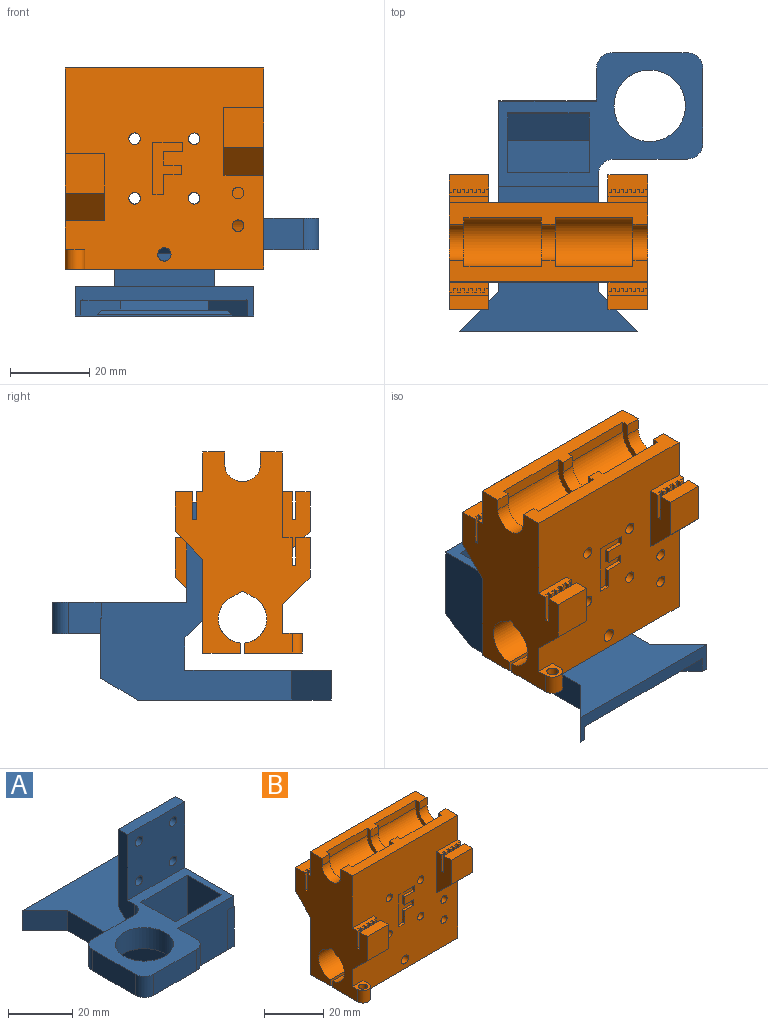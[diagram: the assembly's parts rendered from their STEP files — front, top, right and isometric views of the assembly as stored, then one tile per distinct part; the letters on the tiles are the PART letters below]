
ASSEMBLY  parts=2 mates=1
PART A: 52 faces, bbox 61.4x70.2x49.6 mm
  f0: plane 15.13x2.75mm, normal (0,-1,0), area 40mm2, adj f1,f4,f16,f31,f42,f43
  f1: plane 2.35x0.1mm, normal (0,0,1), area 0.2mm2, adj f0,f4,f12,f43
  f2: plane 49.63x48.05mm, normal (1,0,0), area 828.1mm2, adj f3,f11,f12,f14,f15,f21,f25,f26
  f3: plane 51.4x33.8mm, normal (0,0,1), area 683.6mm2, adj f2,f12,f13,f14,f16,f22,f23,f24
  f4: plane 15.13x0.1mm, normal (1,0,0), area 1.5mm2, adj f0,f1,f12,f30
  f5: plane 15.13x0.1mm, normal (-1,0,0), area 1.5mm2, adj f12,f25,f30,f41
  f6: plane 10x10mm, normal (-0.71,0.71,0), area 61.9mm2, adj f7,f8,f28,f29,f34,f38,f39,f40
  f7: plane 51.13x34mm, normal (0,0,-1), area 853.3mm2, adj f6,f9,f13,f22,f23,f24,f27,f28
  f8: plane 31.51x30.04mm, normal (0,0,1), area 683.5mm2, adj f6,f27,f28,f32,f36,f39
  f9: plane 22x7.11mm, normal (0,0.51,0.86), area 182.2mm2, adj f7,f10,f27,f28
  f10: plane 22x11.17mm, normal (0,0,1), area 245.7mm2, adj f9,f27,f28,f32
  f11: plane 25x8.13mm, normal (0,1,0), area 203.1mm2, adj f2,f16,f26,f37
  f12: plane 24.6x19.13mm, normal (0,-1,0), area 393.3mm2, adj f1,f2,f3,f4,f5,f30,f41,f43
  f13: plane 20.5x19.13mm, normal (0,-1,0), area 392.1mm2, adj f3,f7,f22,f23
  f14: plane 25x25mm, normal (0,-1,0), area 589.7mm2, adj f2,f3,f15,f16,f17,f18,f19,f20
  f15: plane 25x4mm, normal (0,0,1), area 100mm2, adj f2,f14,f16,f21
  f16: plane 49.63x48.05mm, normal (-1,0,0), area 678.9mm2, adj f0,f3,f11,f14,f15,f21,f26,f29
  f17: cylinder r=1.68mm len=4mm, axis (0,1,0), area 42.1mm2, adj f14,f21
  f18: cylinder r=1.68mm len=4mm, axis (0,1,0), area 42.1mm2, adj f14,f21
  f19: cylinder r=1.68mm len=4mm, axis (0,1,0), area 42.1mm2, adj f14,f21
  f20: cylinder r=1.68mm len=4mm, axis (0,1,0), area 42.1mm2, adj f14,f21
  f21: plane 29.5x25mm, normal (0,1,0), area 702.2mm2, adj f2,f15,f16,f17,f18,f19,f20,f37
  f22: plane 19.13x15mm, normal (1,0,0), area 286.9mm2, adj f3,f7,f13,f24
  f23: plane 19.13x15mm, normal (-1,0,0), area 286.9mm2, adj f3,f7,f13,f24
  f24: plane 20.5x19.13mm, normal (0,1,0), area 392.1mm2, adj f3,f7,f22,f23
  f25: plane 15.13x2.75mm, normal (0,-1,0), area 41.6mm2, adj f2,f5,f31,f41
  f26: plane 45x36.85mm, normal (0,0,1), area 1021.3mm2, adj f2,f11,f16,f33,f34,f35
  f27: plane 45.13x4.25mm, normal (1,0,0), area 170.1mm2, adj f7,f8,f9,f10,f32,f36
  f28: plane 45.13x4.25mm, normal (-1,0,0), area 170.1mm2, adj f6,f7,f8,f9,f10,f32
  f29: plane 48.85x45mm, normal (0,0,-1), area 1167.7mm2, adj f2,f6,f16,f31,f33,f34,f35,f36
  f30: plane 19.5x0.1mm, normal (0,0,1), area 1.9mm2, adj f4,f5,f12,f31
  f31: plane 25x9.2mm, normal (0,-0.51,-0.86), area 268mm2, adj f0,f2,f16,f25,f29,f30
  f32: cylinder r=5mm len=22mm, axis (-1,0,0), area 34.9mm2, adj f8,f10,f27,f28
  f33: plane 10x10mm, normal (0.71,-0.71,0), area 106.1mm2, adj f2,f26,f29,f34
  f34: plane 45x7.5mm, normal (0,1,0), area 169.5mm2, adj f6,f26,f29,f33,f35,f36,f40
  f35: plane 10x10mm, normal (-0.71,-0.71,0), area 106.1mm2, adj f16,f26,f29,f34
  f36: plane 10x10mm, normal (0.71,0.71,0), area 61.9mm2, adj f7,f8,f27,f29,f34,f38,f39,f40
  f37: plane 25x4.5mm, normal (0,0.71,-0.71), area 159.1mm2, adj f2,f11,f16,f21
  f38: plane 33.91x0.3mm, normal (0,1,0), area 10.2mm2, adj f6,f29,f36,f39
  f39: plane 33.91x1.2mm, normal (0,0.71,0.71), area 55.5mm2, adj f6,f8,f36,f38
  f40: plane 42x4mm, normal (0,-0.35,-0.94), area 162.3mm2, adj f6,f7,f34,f36
  f41: plane 2.75x0.1mm, normal (0,0,1), area 0.3mm2, adj f2,f5,f12,f25
  f42: plane 30.8x26.8mm, normal (0,0,-1), area 451mm2, adj f0,f16,f43,f44,f45,f46,f47,f48
  f43: plane 8.2x8mm, normal (1,0,0), area 65.2mm2, adj f0,f1,f3,f12,f42,f51
  f44: plane 18.4x8mm, normal (0,1,0), area 147.2mm2, adj f3,f42,f48,f49
  f45: plane 18.8x8mm, normal (-1,0,0), area 150.4mm2, adj f3,f42,f49,f50
  f46: cylinder r=9mm len=18mm, axis (0,0,1), area 452.4mm2, adj f3,f42
  f47: plane 18.8x8mm, normal (0,-1,0), area 150.4mm2, adj f3,f42,f50,f51
  f48: cylinder r=4mm len=8mm, axis (0,0,-1), area 50.3mm2, adj f3,f16,f42,f44
  f49: cylinder r=4mm len=8mm, axis (0,0,-1), area 50.3mm2, adj f3,f42,f44,f45
  f50: cylinder r=4mm len=8mm, axis (0,0,1), area 50.3mm2, adj f3,f42,f45,f47
  f51: cylinder r=4mm len=8mm, axis (0,0,-1), area 50.3mm2, adj f3,f42,f43,f47
PART B: 162 faces, bbox 50x34x50.6 mm
  f0: plane 50.6x50mm, normal (0,-1,0), area 2059.2mm2, adj f1,f6,f7,f8,f22,f24,f25,f40
  f1: plane 50.6x34mm, normal (-1,0,0), area 1020.9mm2, adj f0,f2,f5,f8,f12,f23,f24,f25
  f2: plane 10x4.5mm, normal (0,0,1), area 40.5mm2, adj f1,f91,f92,f114,f115,f116,f117,f118
  f3: plane 17x7mm, normal (-1,0,0), area 88.2mm2, adj f4,f5,f88,f89,f105,f106,f113,f135
  f4: plane 10x4.5mm, normal (0,0,1), area 40.5mm2, adj f3,f22,f89,f93,f94,f95,f96,f97
  f5: plane 50.6x50mm, normal (0,1,0), area 2154.8mm2, adj f1,f3,f12,f22,f23,f88,f90,f91
  f6: plane 10x2.5mm, normal (0,0,1), area 20.5mm2, adj f0,f7,f22,f67,f68,f69,f70,f71
  f7: plane 17x7mm, normal (-1,0,0), area 88.2mm2, adj f0,f6,f42,f43,f44,f79,f80,f87
  f8: plane 10x2.5mm, normal (0,0,1), area 20.5mm2, adj f0,f1,f40,f46,f47,f48,f49,f50
  f9: plane 19.5x3mm, normal (0,-1,0), area 58.5mm2, adj f10,f12,f34,f38
  f10: cylinder r=6.2mm len=19.5mm, axis (-1,0,0), area 379.8mm2, adj f9,f11,f34,f38
  f11: plane 19.5x3mm, normal (0,1,0), area 58.5mm2, adj f10,f25,f34,f38
  f12: plane 50x5.5mm, normal (0,0,1), area 208.7mm2, adj f1,f5,f9,f13,f16,f21,f22,f32
  f13: plane 3.5x3mm, normal (0,-1,0), area 10.5mm2, adj f12,f15,f33,f34
  f14: plane 3.5x3mm, normal (0,1,0), area 10.5mm2, adj f15,f25,f33,f34
  f15: cylinder r=4.5mm len=9mm, axis (-1,0,0), area 49.5mm2, adj f13,f14,f33,f34
  f16: plane 19.5x3mm, normal (0,-1,0), area 58.5mm2, adj f12,f17,f32,f33
  f17: cylinder r=6.2mm len=19.5mm, axis (-1,0,0), area 379.8mm2, adj f16,f18,f32,f33
  f18: plane 19.5x3mm, normal (0,1,0), area 58.5mm2, adj f17,f25,f32,f33
  f19: cylinder r=4.5mm len=9mm, axis (-1,0,0), area 53mm2, adj f20,f21,f22,f32
  f20: plane 3.75x3mm, normal (0,1,0), area 11.2mm2, adj f19,f22,f25,f32
  f21: plane 3.75x3mm, normal (0,-1,0), area 11.2mm2, adj f12,f19,f22,f32
  f22: plane 50.6x34mm, normal (1,0,0), area 995.8mm2, adj f0,f4,f5,f6,f12,f19,f20,f21
  f23: plane 50x9.5mm, normal (0,0,-1), area 475mm2, adj f1,f5,f22,f30
  f24: plane 50x14.5mm, normal (0,0,-1), area 490.7mm2, adj f0,f1,f22,f31,f159,f160,f161
  f25: plane 50x5.5mm, normal (0,0,1), area 208.7mm2, adj f0,f1,f11,f14,f18,f20,f22,f32
  f26: plane 50x2.45mm, normal (0,-0.5,-0.87), area 141.3mm2, adj f1,f22,f27,f29
  f27: cylinder r=6.1mm len=50mm, axis (-1,0,0), area 791.2mm2, adj f1,f22,f26,f30,f139
  f28: cylinder r=6.1mm len=50mm, axis (-1,0,0), area 784.5mm2, adj f1,f22,f29,f31,f138,f143,f144
  f29: plane 50x2.45mm, normal (0,0.5,-0.87), area 141.3mm2, adj f1,f22,f26,f28
  f30: plane 50x2.52mm, normal (0,-1,0), area 125.2mm2, adj f1,f22,f23,f27,f139
  f31: plane 50x2.52mm, normal (0,1,0), area 125.2mm2, adj f1,f22,f24,f28,f138
  f32: plane 12.4x9.2mm, normal (-1,0,0), area 38.8mm2, adj f12,f16,f17,f18,f19,f20,f21,f25
  f33: plane 12.4x9.2mm, normal (1,0,0), area 38.8mm2, adj f12,f13,f14,f15,f16,f17,f18,f25
  f34: plane 12.4x9.2mm, normal (-1,0,0), area 38.8mm2, adj f9,f10,f11,f12,f13,f14,f15,f25
  f35: plane 3.75x3mm, normal (0,-1,0), area 11.2mm2, adj f1,f12,f37,f38
  f36: plane 3.75x3mm, normal (0,1,0), area 11.2mm2, adj f1,f25,f37,f38
  f37: cylinder r=4.5mm len=9mm, axis (-1,0,0), area 53mm2, adj f1,f35,f36,f38
  f38: plane 12.4x9.2mm, normal (1,0,0), area 38.8mm2, adj f9,f10,f11,f12,f25,f35,f36,f37
  f39: plane 10x3.6mm, normal (0,0,1), area 36mm2, adj f1,f40,f41,f59
  f40: plane 17x7mm, normal (1,0,0), area 81.9mm2, adj f0,f8,f39,f41,f45,f59,f60,f66
  f41: plane 10x10mm, normal (0,-1,0), area 100mm2, adj f1,f39,f40,f45
  f42: plane 10x3.6mm, normal (0,0,1), area 36mm2, adj f7,f22,f43,f80
  f43: plane 10x10mm, normal (0,-1,0), area 100mm2, adj f7,f22,f42,f44
  f44: plane 10x7mm, normal (0,-0.71,-0.71), area 99mm2, adj f0,f7,f22,f43
  f45: plane 10x7mm, normal (0,-0.71,-0.71), area 99mm2, adj f0,f1,f40,f41
  f46: plane 7x1mm, normal (0,-1,0), area 7mm2, adj f8,f47,f65,f66
  f47: plane 7x0.9mm, normal (-1,0,0), area 6.3mm2, adj f8,f46,f48,f66
  f48: plane 7x1mm, normal (0,-1,0), area 7mm2, adj f8,f47,f49,f66
  f49: plane 7x0.9mm, normal (1,0,0), area 6.3mm2, adj f8,f48,f50,f66
  f50: plane 7x1mm, normal (0,-1,0), area 7mm2, adj f8,f49,f51,f66
  f51: plane 7x0.9mm, normal (-1,0,0), area 6.3mm2, adj f8,f50,f52,f66
  f52: plane 7x1mm, normal (0,-1,0), area 7mm2, adj f8,f51,f53,f66
  f53: plane 7x0.9mm, normal (1,0,0), area 6.3mm2, adj f8,f52,f54,f66
  f54: plane 7x1mm, normal (0,-1,0), area 7mm2, adj f8,f53,f55,f66
  f55: plane 7x0.9mm, normal (-1,0,0), area 6.3mm2, adj f8,f54,f56,f66
  f56: plane 7x1mm, normal (0,-1,0), area 7mm2, adj f8,f55,f57,f66
  f57: plane 7x0.9mm, normal (1,0,0), area 6.3mm2, adj f8,f56,f58,f66
  f58: plane 7x1mm, normal (0,-1,0), area 7mm2, adj f1,f8,f57,f66
  f59: plane 10x7mm, normal (0,1,0), area 70mm2, adj f1,f39,f40,f66
  f60: plane 7x1mm, normal (0,-1,0), area 7mm2, adj f8,f40,f61,f66
  f61: plane 7x0.9mm, normal (1,0,0), area 6.3mm2, adj f8,f60,f62,f66
  f62: plane 7x1mm, normal (0,-1,0), area 7mm2, adj f8,f61,f63,f66
  f63: plane 7x0.9mm, normal (-1,0,0), area 6.3mm2, adj f8,f62,f64,f66
  f64: plane 7x1mm, normal (0,-1,0), area 7mm2, adj f8,f63,f65,f66
  f65: plane 7x0.9mm, normal (1,0,0), area 6.3mm2, adj f8,f46,f64,f66
  f66: plane 10x1.8mm, normal (0,0,1), area 13.5mm2, adj f1,f40,f46,f47,f48,f49,f50,f51
  f67: plane 7x1mm, normal (0,-1,0), area 7mm2, adj f6,f68,f86,f87
  f68: plane 7x0.9mm, normal (-1,0,0), area 6.3mm2, adj f6,f67,f69,f87
  f69: plane 7x1mm, normal (0,-1,0), area 7mm2, adj f6,f68,f70,f87
  f70: plane 7x0.9mm, normal (1,0,0), area 6.3mm2, adj f6,f69,f71,f87
  f71: plane 7x1mm, normal (0,-1,0), area 7mm2, adj f6,f70,f72,f87
  f72: plane 7x0.9mm, normal (-1,0,0), area 6.3mm2, adj f6,f71,f73,f87
  f73: plane 7x1mm, normal (0,-1,0), area 7mm2, adj f6,f72,f74,f87
  f74: plane 7x0.9mm, normal (1,0,0), area 6.3mm2, adj f6,f73,f75,f87
  f75: plane 7x1mm, normal (0,-1,0), area 7mm2, adj f6,f74,f76,f87
  f76: plane 7x0.9mm, normal (-1,0,0), area 6.3mm2, adj f6,f75,f77,f87
  f77: plane 7x1mm, normal (0,-1,0), area 7mm2, adj f6,f76,f78,f87
  f78: plane 7x0.9mm, normal (1,0,0), area 6.3mm2, adj f6,f77,f79,f87
  f79: plane 7x1mm, normal (0,-1,0), area 7mm2, adj f6,f7,f78,f87
  f80: plane 10x7mm, normal (0,1,0), area 70mm2, adj f7,f22,f42,f87
  f81: plane 7x1mm, normal (0,-1,0), area 7mm2, adj f6,f22,f82,f87
  f82: plane 7x0.9mm, normal (1,0,0), area 6.3mm2, adj f6,f81,f83,f87
  f83: plane 7x1mm, normal (0,-1,0), area 7mm2, adj f6,f82,f84,f87
  f84: plane 7x0.9mm, normal (-1,0,0), area 6.3mm2, adj f6,f83,f85,f87
  f85: plane 7x1mm, normal (0,-1,0), area 7mm2, adj f6,f84,f86,f87
  f86: plane 7x0.9mm, normal (1,0,0), area 6.3mm2, adj f6,f67,f85,f87
  f87: plane 10x1.8mm, normal (0,0,1), area 13.5mm2, adj f7,f22,f67,f68,f69,f70,f71,f72
  f88: plane 10x1.6mm, normal (0,0,1), area 16mm2, adj f3,f5,f22,f106
  f89: plane 10x10mm, normal (0,1,0), area 100mm2, adj f3,f4,f22,f135
  f90: plane 10x1.6mm, normal (0,0,1), area 16mm2, adj f1,f5,f91,f127
  f91: plane 17x7mm, normal (1,0,0), area 81.9mm2, adj f2,f5,f90,f92,f127,f128,f134,f136
  f92: plane 10x10mm, normal (0,1,0), area 100mm2, adj f1,f2,f91,f136
  f93: plane 7x1mm, normal (0,-1,0), area 7mm2, adj f4,f94,f112,f113
  f94: plane 7x0.9mm, normal (-1,0,0), area 6.3mm2, adj f4,f93,f95,f113
  f95: plane 7x1mm, normal (0,-1,0), area 7mm2, adj f4,f94,f96,f113
  f96: plane 7x0.9mm, normal (1,0,0), area 6.3mm2, adj f4,f95,f97,f113
  f97: plane 7x1mm, normal (0,-1,0), area 7mm2, adj f4,f96,f98,f113
  f98: plane 7x0.9mm, normal (-1,0,0), area 6.3mm2, adj f4,f97,f99,f113
  f99: plane 7x1mm, normal (0,-1,0), area 7mm2, adj f4,f98,f100,f113
  f100: plane 7x0.9mm, normal (1,0,0), area 6.3mm2, adj f4,f99,f101,f113
  f101: plane 7x1mm, normal (0,-1,0), area 7mm2, adj f4,f100,f102,f113
  f102: plane 7x0.9mm, normal (-1,0,0), area 6.3mm2, adj f4,f101,f103,f113
  f103: plane 7x1mm, normal (0,-1,0), area 7mm2, adj f4,f102,f104,f113
  f104: plane 7x0.9mm, normal (1,0,0), area 6.3mm2, adj f4,f103,f105,f113
  f105: plane 7x1mm, normal (0,-1,0), area 7mm2, adj f3,f4,f104,f113
  f106: plane 10x7mm, normal (0,1,0), area 70mm2, adj f3,f22,f88,f113
  f107: plane 7x1mm, normal (0,-1,0), area 7mm2, adj f4,f22,f108,f113
  f108: plane 7x0.9mm, normal (1,0,0), area 6.3mm2, adj f4,f107,f109,f113
  f109: plane 7x1mm, normal (0,-1,0), area 7mm2, adj f4,f108,f110,f113
  f110: plane 7x0.9mm, normal (-1,0,0), area 6.3mm2, adj f4,f109,f111,f113
  f111: plane 7x1mm, normal (0,-1,0), area 7mm2, adj f4,f110,f112,f113
  f112: plane 7x0.9mm, normal (1,0,0), area 6.3mm2, adj f4,f93,f111,f113
  f113: plane 10x1.8mm, normal (0,0,1), area 13.5mm2, adj f3,f22,f93,f94,f95,f96,f97,f98
  f114: plane 7x1mm, normal (0,-1,0), area 7mm2, adj f2,f115,f133,f134
  f115: plane 7x0.9mm, normal (-1,0,0), area 6.3mm2, adj f2,f114,f116,f134
  f116: plane 7x1mm, normal (0,-1,0), area 7mm2, adj f2,f115,f117,f134
  f117: plane 7x0.9mm, normal (1,0,0), area 6.3mm2, adj f2,f116,f118,f134
  f118: plane 7x1mm, normal (0,-1,0), area 7mm2, adj f2,f117,f119,f134
  f119: plane 7x0.9mm, normal (-1,0,0), area 6.3mm2, adj f2,f118,f120,f134
  f120: plane 7x1mm, normal (0,-1,0), area 7mm2, adj f2,f119,f121,f134
  f121: plane 7x0.9mm, normal (1,0,0), area 6.3mm2, adj f2,f120,f122,f134
  f122: plane 7x1mm, normal (0,-1,0), area 7mm2, adj f2,f121,f123,f134
  f123: plane 7x0.9mm, normal (-1,0,0), area 6.3mm2, adj f2,f122,f124,f134
  f124: plane 7x1mm, normal (0,-1,0), area 7mm2, adj f2,f123,f125,f134
  f125: plane 7x0.9mm, normal (1,0,0), area 6.3mm2, adj f2,f124,f126,f134
  f126: plane 7x1mm, normal (0,-1,0), area 7mm2, adj f1,f2,f125,f134
  f127: plane 10x7mm, normal (0,1,0), area 70mm2, adj f1,f90,f91,f134
  f128: plane 7x1mm, normal (0,-1,0), area 7mm2, adj f2,f91,f129,f134
  f129: plane 7x0.9mm, normal (1,0,0), area 6.3mm2, adj f2,f128,f130,f134
  f130: plane 7x1mm, normal (0,-1,0), area 7mm2, adj f2,f129,f131,f134
  f131: plane 7x0.9mm, normal (-1,0,0), area 6.3mm2, adj f2,f130,f132,f134
  f132: plane 7x1mm, normal (0,-1,0), area 7mm2, adj f2,f131,f133,f134
  f133: plane 7x0.9mm, normal (1,0,0), area 6.3mm2, adj f2,f114,f132,f134
  f134: plane 10x1.8mm, normal (0,0,1), area 13.5mm2, adj f1,f91,f114,f115,f116,f117,f118,f119
  f135: plane 10x7mm, normal (0,0.71,-0.71), area 99mm2, adj f3,f5,f22,f89
  f136: plane 10x7mm, normal (0,0.71,-0.71), area 99mm2, adj f1,f5,f91,f92
  f137: cylinder r=1.45mm len=20mm, axis (0,-1,0), area 182.2mm2, adj f0,f5
  f138: cylinder r=1.68mm len=9.5mm, axis (0,-1,0), area 73.2mm2, adj f0,f28,f31
  f139: cylinder r=1.68mm len=9.5mm, axis (0,-1,0), area 73.1mm2, adj f5,f27,f30
  f140: cylinder r=1.45mm len=20mm, axis (0,-1,0), area 182.2mm2, adj f0,f5
  f141: cylinder r=1.45mm len=20mm, axis (0,-1,0), area 182.2mm2, adj f0,f5
  f142: cylinder r=1.45mm len=20mm, axis (0,-1,0), area 182.2mm2, adj f0,f5
  f143: cylinder r=1.45mm len=5mm, axis (0,-1,0), area 40.4mm2, adj f0,f28,f144
  f144: plane 1.64x0.26mm, normal (0,-1,0), area 0.3mm2, adj f28,f143
  f145: cylinder r=1.45mm len=5mm, axis (0,-1,0), area 45.6mm2, adj f0,f146
  f146: plane 2.9x2.9mm, normal (0,-1,0), area 6.6mm2, adj f145
  f147: plane 2.75x1mm, normal (0,0,1), area 2.7mm2, adj f0,f148,f156,f157
  f148: plane 5.2x1mm, normal (-1,0,0), area 5.2mm2, adj f0,f147,f149,f157
  f149: plane 4.47x1mm, normal (0,0,1), area 4.5mm2, adj f0,f148,f150,f157
  f150: plane 2.28x1mm, normal (-1,0,0), area 2.3mm2, adj f0,f149,f151,f157
  f151: plane 4.47x1mm, normal (0,0,-1), area 4.5mm2, adj f0,f150,f152,f157
  f152: plane 3.39x1mm, normal (-1,0,0), area 3.4mm2, adj f0,f151,f153,f157
  f153: plane 4.8x1mm, normal (0,0,1), area 4.8mm2, adj f0,f152,f154,f157
  f154: plane 2.29x1mm, normal (-1,0,0), area 2.3mm2, adj f0,f153,f155,f157
  f155: plane 7.55x1mm, normal (0,0,-1), area 7.5mm2, adj f0,f154,f156,f157
  f156: plane 13.17x1mm, normal (1,0,0), area 13.2mm2, adj f0,f147,f155,f157
  f157: plane 13.17x7.55mm, normal (0,-1,0), area 57.3mm2, adj f147,f148,f149,f150,f151,f152,f153,f154
  f158: plane 5x5mm, normal (0,0,1), area 15.7mm2, adj f0,f1,f159,f160,f161
  f159: plane 5x2.5mm, normal (1,0,0), area 12.5mm2, adj f0,f24,f158,f161
  f160: cylinder r=1.45mm len=5mm, axis (0,0,1), area 45.6mm2, adj f24,f158
  f161: cylinder r=2.5mm len=5mm, axis (0,0,-1), area 39.3mm2, adj f1,f24,f158,f159
PLACE A rot(axis=(0,0,1),180deg) t=(-42.87,0.02,8.22)mm
PLACE B rot(axis=(0,0,-1),0deg) t=(-69.19,-19.98,-20.42)mm
MATE fastened B.f137 <-> A.f18  axis (0,1,0) through (-36.69,0.02,12.38)mm
